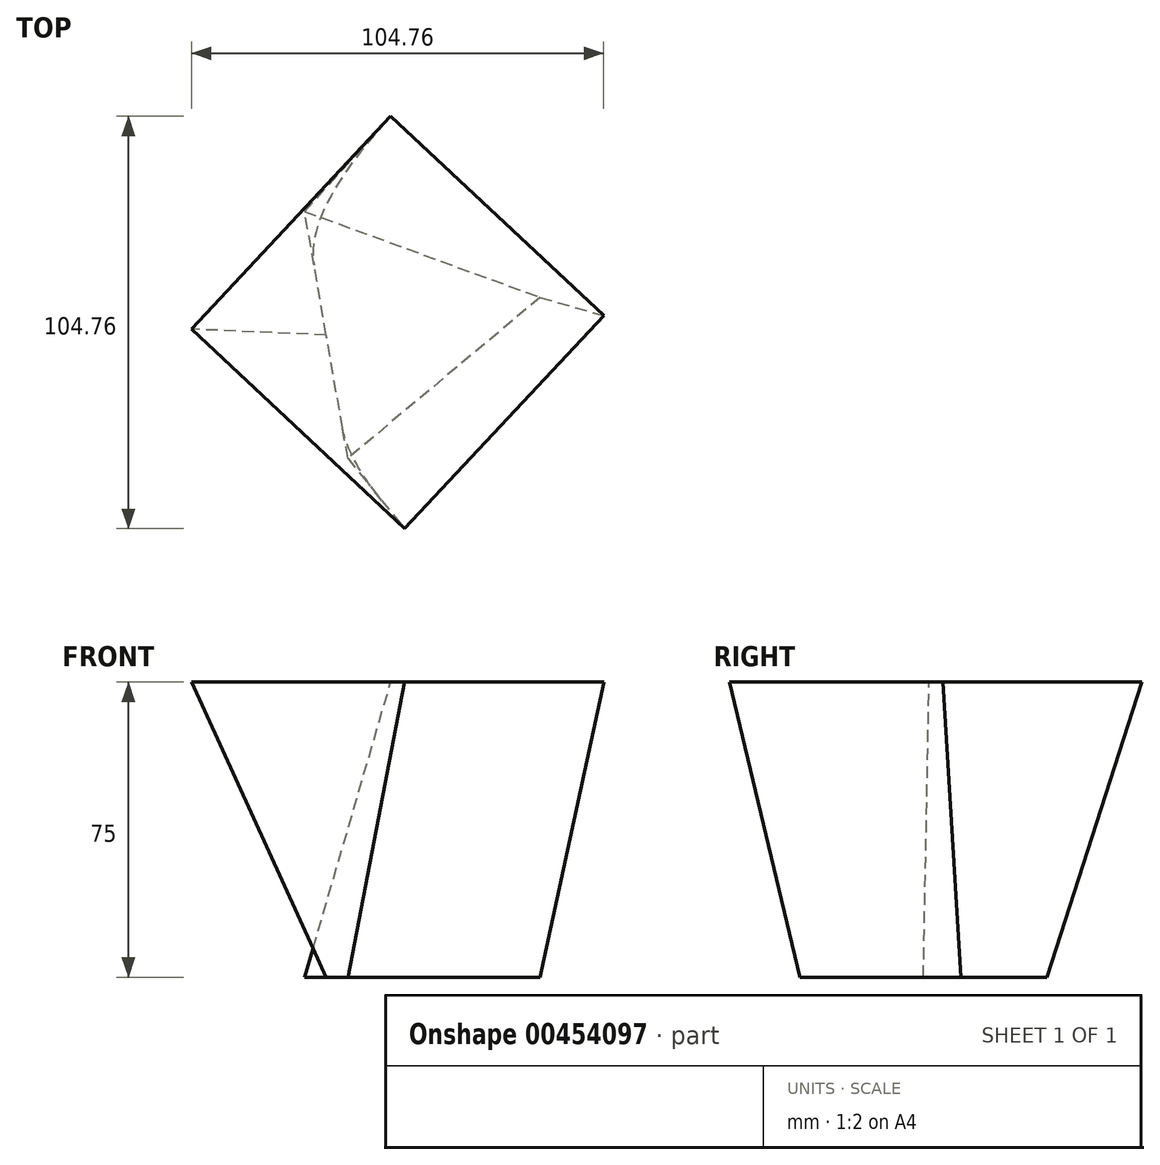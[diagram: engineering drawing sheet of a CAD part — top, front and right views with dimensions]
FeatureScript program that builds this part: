
annotation { "Feature Type Name" : "Feature", "Feature Type Description" : "" }
export const myFeature = defineFeature(function(context is Context, id is Id, definition is map)
    precondition{}
    {
        {
            var Q0;
            Q0=qCreatedBy(makeId("Top.planeOp"),FACE);
            var sketch = newSketch(context, id + "F0", { "sketchPlane" : qUnion([Q0])});
            skCircle(sketch, "E0.cCircle", {"center": v(0, 0) * mm, "radius": 18.39 * mm, "construction": true});
            skLineSegment(sketch, "E0.0", {"start": v(36.23, 6.34) * mm, "end": v(-12.63, -34.54) * mm});
            skLineSegment(sketch, "E0.1", {"start": v(-12.63, -34.54) * mm, "end": v(-23.6, 28.2) * mm});
            skLineSegment(sketch, "E0.2", {"start": v(-23.6, 28.2) * mm, "end": v(36.23, 6.34) * mm});
            skPoint(sketch, "E0.0.midPoint", {"position": v(11.8, -14.1) * mm});
            skSolve(sketch);
        }
        {
            var Q0;
            Q0=qCreatedBy(makeId("Top.planeOp"),FACE);
            cPlane(context, id + "F1", {"entities" : qUnion([Q0]), "cplaneType" : CPlaneType.OFFSET, "offset" : 75 * mm, "width" : 152.4 * mm, "height" : 152.4 * mm});
        }
        {
            var Q0;
            Q0=qCreatedBy(id+"F1.planeOp",FACE);
            var sketch = newSketch(context, id + "F2", { "sketchPlane" : qUnion([Q0])});
            skCircle(sketch, "E1.cCircle", {"center": v(0, 0) * mm, "radius": 37.06 * mm, "construction": true});
            skLineSegment(sketch, "E1.0", {"start": v(52.38, 1.73) * mm, "end": v(1.73, -52.38) * mm});
            skLineSegment(sketch, "E1.1", {"start": v(1.73, -52.38) * mm, "end": v(-52.38, -1.73) * mm});
            skLineSegment(sketch, "E1.2", {"start": v(-52.38, -1.73) * mm, "end": v(-1.73, 52.38) * mm});
            skLineSegment(sketch, "E1.3", {"start": v(-1.73, 52.38) * mm, "end": v(52.38, 1.73) * mm});
            skPoint(sketch, "E1.0.midPoint", {"position": v(27.05, -25.33) * mm});
            skSolve(sketch);
        }
        {
            var Q0;
            Q0=makeQuery(id+"F0.imprint","IMPRINT",FACE,{"disambiguationData":[TD([[makeQuery(id+"F0.imprint","IMPRINT",EDGE,{"derivedFrom":sQuery(id+"F0.wireOp",EDGE,"E0.0")}),-1.0]])]});
            var Q1;
            Q1=makeQuery(id+"F2.imprint","IMPRINT",FACE,{"disambiguationData":[TD([[makeQuery(id+"F2.imprint","IMPRINT",EDGE,{"derivedFrom":sQuery(id+"F2.wireOp",EDGE,"E1.0")}),-1.0]])]});
            loft(context, id + "F3", {"sheetProfilesArray" : [{ "sheetProfileEntities" : qUnion([Q0]) }, { "sheetProfileEntities" : qUnion([Q1]) }]});
        }
    });
